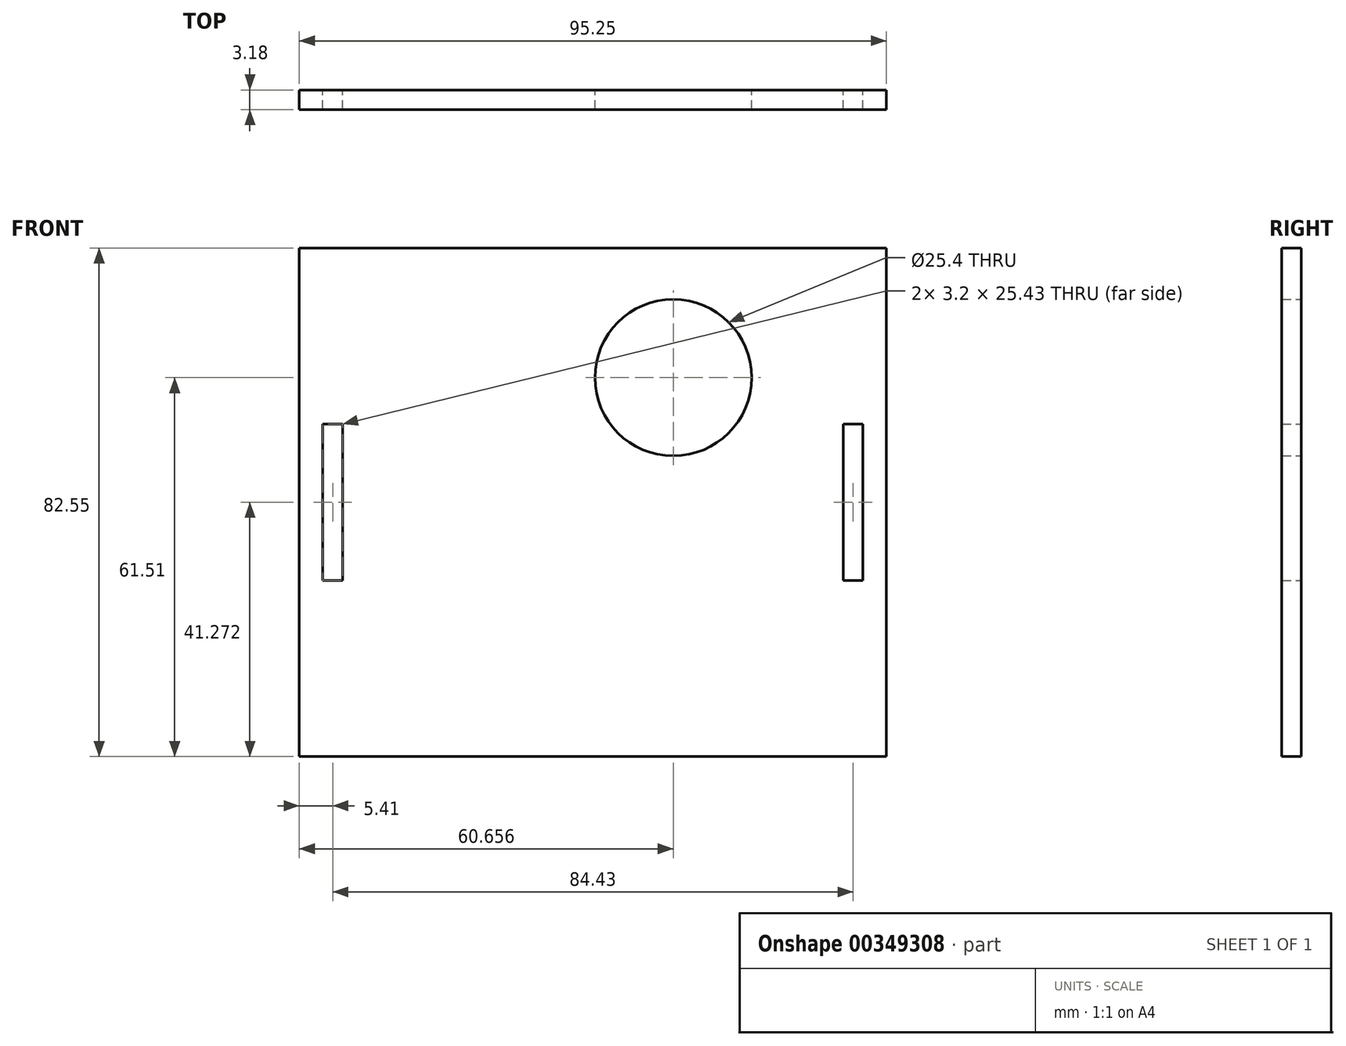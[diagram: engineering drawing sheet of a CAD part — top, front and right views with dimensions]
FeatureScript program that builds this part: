
annotation { "Feature Type Name" : "Feature", "Feature Type Description" : "" }
export const myFeature = defineFeature(function(context is Context, id is Id, definition is map)
    precondition{}
    {
        {
            var Q0;
            Q0=qCreatedBy(makeId("Front.planeOp"),FACE);
            var sketch = newSketch(context, id + "F0", { "sketchPlane" : qUnion([Q0])});
            skLineSegment(sketch, "E0.bottom", {"start": v(-95.23, 34.8) * mm, "end": v(0.02, 34.8) * mm});
            skLineSegment(sketch, "E0.top", {"start": v(-95.23, -47.74) * mm, "end": v(0.02, -47.74) * mm});
            skLineSegment(sketch, "E0.left", {"start": v(-95.23, 34.8) * mm, "end": v(-95.23, -47.74) * mm});
            skLineSegment(sketch, "E0.right", {"start": v(0.02, 34.8) * mm, "end": v(0.02, -47.74) * mm});
            skCircle(sketch, "E1", {"center": v(-34.57, 13.77) * mm, "radius": 12.7 * mm});
            skLineSegment(sketch, "E2.bottom", {"start": v(-91.42, 6.24) * mm, "end": v(-88.22, 6.24) * mm});
            skLineSegment(sketch, "E2.top", {"start": v(-91.42, -19.18) * mm, "end": v(-88.22, -19.18) * mm});
            skLineSegment(sketch, "E2.left", {"start": v(-91.42, 6.24) * mm, "end": v(-91.42, -19.18) * mm});
            skLineSegment(sketch, "E2.right", {"start": v(-88.22, 6.24) * mm, "end": v(-88.22, -19.18) * mm});
            skPoint(sketch, "E3", {"position": v(-88.22, -6.47) * mm});
            skPoint(sketch, "E4", {"position": v(-95.23, -6.47) * mm});
            skPoint(sketch, "E5", {"position": v(0.02, -6.47) * mm});
            skLineSegment(sketch, "E6.bottom", {"start": v(-7, 6.24) * mm, "end": v(-3.8, 6.24) * mm});
            skLineSegment(sketch, "E6.top", {"start": v(-7, -19.18) * mm, "end": v(-3.8, -19.18) * mm});
            skLineSegment(sketch, "E6.left", {"start": v(-7, 6.24) * mm, "end": v(-7, -19.18) * mm});
            skLineSegment(sketch, "E6.right", {"start": v(-3.8, 6.24) * mm, "end": v(-3.8, -19.18) * mm});
            skPoint(sketch, "E7", {"position": v(-7, -6.47) * mm});
            skLineSegment(sketch, "E8.bottom", {"start": v(-80.43, 34.8) * mm, "end": v(-55, 34.8) * mm});
            skLineSegment(sketch, "E8.top", {"start": v(-80.43, 37.98) * mm, "end": v(-55, 37.98) * mm});
            skLineSegment(sketch, "E8.left", {"start": v(-80.43, 34.8) * mm, "end": v(-80.43, 37.98) * mm});
            skLineSegment(sketch, "E8.right", {"start": v(-55, 34.8) * mm, "end": v(-55, 37.98) * mm});
            skLineSegment(sketch, "E9.bottom", {"start": v(-40.2, 34.8) * mm, "end": v(-14.78, 34.8) * mm});
            skLineSegment(sketch, "E9.top", {"start": v(-40.2, 37.98) * mm, "end": v(-14.78, 37.98) * mm});
            skLineSegment(sketch, "E9.left", {"start": v(-40.2, 34.8) * mm, "end": v(-40.2, 37.98) * mm});
            skLineSegment(sketch, "E9.right", {"start": v(-14.78, 34.8) * mm, "end": v(-14.78, 37.98) * mm});
            skLineSegment(sketch, "E10.bottom", {"start": v(-80.43, -47.74) * mm, "end": v(-55, -47.74) * mm});
            skLineSegment(sketch, "E10.top", {"start": v(-80.43, -50.92) * mm, "end": v(-55, -50.92) * mm});
            skLineSegment(sketch, "E10.left", {"start": v(-80.43, -47.74) * mm, "end": v(-80.43, -50.92) * mm});
            skLineSegment(sketch, "E10.right", {"start": v(-55, -47.74) * mm, "end": v(-55, -50.92) * mm});
            skLineSegment(sketch, "E11.bottom", {"start": v(-40.2, -47.74) * mm, "end": v(-14.78, -47.74) * mm});
            skLineSegment(sketch, "E11.top", {"start": v(-40.2, -50.92) * mm, "end": v(-14.78, -50.92) * mm});
            skLineSegment(sketch, "E11.left", {"start": v(-40.2, -47.74) * mm, "end": v(-40.2, -50.92) * mm});
            skLineSegment(sketch, "E11.right", {"start": v(-14.78, -47.74) * mm, "end": v(-14.78, -50.92) * mm});
            skSolve(sketch);
        }
        {
            var Q0;
            Q0=makeQuery(id+"F0.imprint","IMPRINT",FACE,{"disambiguationData":[TD([[makeQuery(id+"F0.imprint","IMPRINT",EDGE,{"derivedFrom":sQuery(id+"F0.wireOp",EDGE,"E0.bottom")}),-1.0]])]});
            var Q1;
            Q1=makeQuery(id+"F0.imprint","IMPRINT",FACE,{"disambiguationData":[TD([[makeQuery(id+"F0.imprint","IMPRINT",EDGE,{"derivedFrom":sQuery(id+"F0.wireOp",EDGE,"E8.bottom")}),1.0]])]});
            var Q2;
            Q2=makeQuery(id+"F0.imprint","IMPRINT",FACE,{"disambiguationData":[TD([[makeQuery(id+"F0.imprint","IMPRINT",EDGE,{"derivedFrom":sQuery(id+"F0.wireOp",EDGE,"E9.bottom")}),1.0]])]});
            var Q3;
            Q3=makeQuery(id+"F0.imprint","IMPRINT",FACE,{"disambiguationData":[TD([[makeQuery(id+"F0.imprint","IMPRINT",EDGE,{"derivedFrom":sQuery(id+"F0.wireOp",EDGE,"E11.bottom")}),-1.0]])]});
            var Q4;
            Q4=makeQuery(id+"F0.imprint","IMPRINT",FACE,{"disambiguationData":[TD([[makeQuery(id+"F0.imprint","IMPRINT",EDGE,{"derivedFrom":sQuery(id+"F0.wireOp",EDGE,"E10.bottom")}),-1.0]])]});
            extrude(context, id + "F1", {"entities" : qUnion([Q0, Q1, Q2, Q3, Q4]), "depth" : 3.17 * mm});
        }
    });
